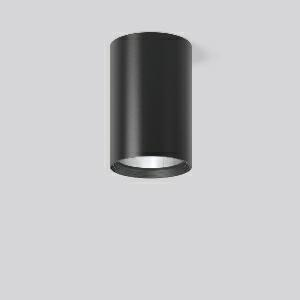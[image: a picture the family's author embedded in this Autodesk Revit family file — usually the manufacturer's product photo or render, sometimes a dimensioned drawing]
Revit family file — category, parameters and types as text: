
# Revit family: heledon_maxi_a_931217_003_2_2f77
name_source: partatom
category: Lighting Fixtures
units: mm (PartAtom-declared; Revit-internal decimal feet)

## family parameters
Cut with Voids When Loaded = No
Host = Face
Light Source = No
Part Type = Normal
Room Calculation Point = No
Round Connector Dimension = Use Diameter
Shared = No

## types (1)
- HELEDON maxi A (1 x LED Modul 927, 3150 lm, 2700)
    Apparent Load = 25 VA
    Approval mark = CE
    CIE Flux Codes = 100 100 100 100 100
    Color Rendering = 92
    Color Temperature = 2700
    Default Elevation = 1800 mm
    Description = Series: HELEDON maxi
Cylindrical surface-mounted downlight. Housing: die-cast aluminium, powder-coated. Internal ceiling frame polycarbonate with bayonet mounting. Black plastic ring and recessed LED to prevent glare from the side. Optical assembly with reflector made of MIRO-Silver with 98% total light reflection for outstanding efficiency - can be changed without tools. Best colour rendering index Ra>90. Suitable for Ceiling mounting. Easy installation with a separate ceiling frame with bayonet mounting and plug connection. Driver integrated. Connected via plug-in connector. High quality converter without flickering and stroboscopic effect. The following accessories can be mounted without use of tools: interchangeable lenses, decorative glasses, honeycomb louvre, clear and frosted diffusers, white interchangeable plastic ring. 
Colour: deep black, matt (RAL 9005)
Diameter: 123 mm
Height: 183 mm
Lamp: LED
Socket: without socket
Colour temperature: 2700K
Colour rendering index (CRI): 92
System power: 25 W
Rated luminous flux: 3150 lm
Luminous efficiency: 126 lm/W
Control gear: Regulated power supply
Protection class: I
Type of protection: IP 20
    Height = 183 mm
    Lamp = 1 x LED Modul 927
    Lamp Light Flux = 3150 lm
    Lamp count = 1
    Length = 123 mm
    Lifetime = 50000 h
    Luminous efficacy = 126 lm/W
    Manufacturer = RZB
    ModVariant = No
    Model = 931217.003.2
    Mounting Place = Ceiling
    Mounting Type = Surface mounted
    Number of Poles = 1
    OnlyDefault = Yes
    Power Factor = 1
    Product Name = HELEDON maxi A
    Product group = Surface mounted downlights
    ProductGroupID = 302
    Protection Class = Protection class I
    Protection Degree = IP 20
    RLX_Detail_Level = 1
    RLX_Emergency_Light_Flux = 0 lm
    RLX_Emergency_Type = 0
    RLX_Emergency_Type_DB = No
    RlxData = <blob elided: 96829 chars, md5=3e262863>
    Socket = socket
    Standby Power = 0 W
    System Light Flux = 3150 lm
    System Power = 25 W
    Type Comments = Product without accessories
    Type Image = 931192.003.jpg
    URL = http://relux.com
    VarID = ---
    Voltage = 230 V
    Voltage Range = 220-240 V
    Weight = 0.00 kg
    Width = 0 mm  [stored 0 ft]

note: [stored X ft] marks values corroborated as IEEE doubles in the binary element streams (Revit-internal decimal feet)

## geometry (parser evidence)
native form markers: Blend x4, Sweep x10
no freeform markers — native parametric forms only
